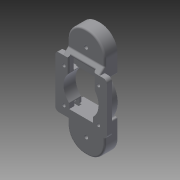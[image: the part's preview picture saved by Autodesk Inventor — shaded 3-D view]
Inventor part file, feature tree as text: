
AUTODESK INVENTOR PART (.ipt)
format: ipt  version: 2014 (Build 180170000, 170)  size: 476,160 bytes
history: native  units: in
note: dims shown in document units (in); Inventor stores cm internally (conversion verified against a paired STEP export)
features: extrude x10, sketch x10, reference x9, fillet x6, projected_geometry x2, plane x1, chamfer x1
ambient origin geometry x8: Origin, YZ Plane, XZ Plane, XY Plane, X Axis, Y Axis, Z Axis, Center Point
bodies: Solid1 (feature_tree)
feature tree (39):
  plane  "Work Plane1"
  extrude  "Extrusion1"  Depth=3.73in
  extrude  "Extrusion3"  Depth=0.864in
  extrude  "Extrusion5"  Depth=0.239in
  extrude  "Extrusion6"  Depth=1.1811in
  extrude  "Extrusion7"  Depth=0.1181in
  extrude  "Extrusion8"  Depth=0.1181in
  extrude  "Extrusion10"  Depth=0.1732in TaperAngle=0.0deg
  extrude  "Extrusion11"  Depth=0.1732in
  fillet  "Fillet1"  Radius=0.125in
  extrude  "Extrusion12"  Depth=0.125in
  chamfer  "Chamfer1"  Distance=0.3in
  fillet  "Fillet2"  Radius=0.125in
  fillet  "Fillet3"  Radius=0.25in
  fillet  "Fillet4"  Radius=0.125in
  fillet  "Fillet5"  Radius=0.125in
  extrude  "Extrusion13"  Depth=0.0394in TaperAngle=0.0deg
  fillet  "Fillet6"  Radius=0.18in
  sketch  "Sketch1"  dims[d0=1.27in d1=3.73in]
  reference  "Reference1"
  sketch  "Sketch2"  dims[d2=0.2in d3=0.0in d4=0.864in]
  reference  "Reference2"
  reference  "Reference3"
  reference  "Reference4"
  reference  "Reference5"
  reference  "Reference6"
  reference  "Reference7"
  reference  "Reference8"
  reference  "Reference9"
  projected_geometry  "Projected Loop1"
  sketch  "Sketch4"  dims[d7=0.239in d8=0.0in d9=1.7717in]
  sketch  "Sketch5"  dims[d10=1.7717in d11=1.1811in]
  sketch  "Sketch6"  dims[d12=1.1811in d13=0.1181in]
  sketch  "Sketch7"  dims[d14=0.1181in d15=0.1181in]
  sketch  "Sketch8"  dims[d16=0.1181in d19=0.1732in d20=0.0in]
  projected_geometry  "Projected Loop2"
  sketch  "Sketch9"  dims[d21=0.1732in d22=0.0in d23=0.125in d25=0.125in]
  sketch  "Sketch10"  dims[d26=0.18in d27=0.125in]
  sketch  "Sketch11"  dims[d28=0.25in d29=0.3in d30=0.0in d31=0.125in d32=0.25in d33=0.125in d34=0.125in d35=0.3in d36=0.0in d37=0.18in d38=0.1339in d39=0.1339in d42=0.0118in d43=0.0in d44=1.2in d45=0.0in d46=0.0in d47=0.125in d48=0.173in d49=0.173in d50=0.0in d51=0.173in d52=0.125in d53=45.0deg d54=0.05in d55=0.6in d56=0.06in d57=0.06in d58=0.15in d59=1.0in d60=0.0in d61=0.0394in]
